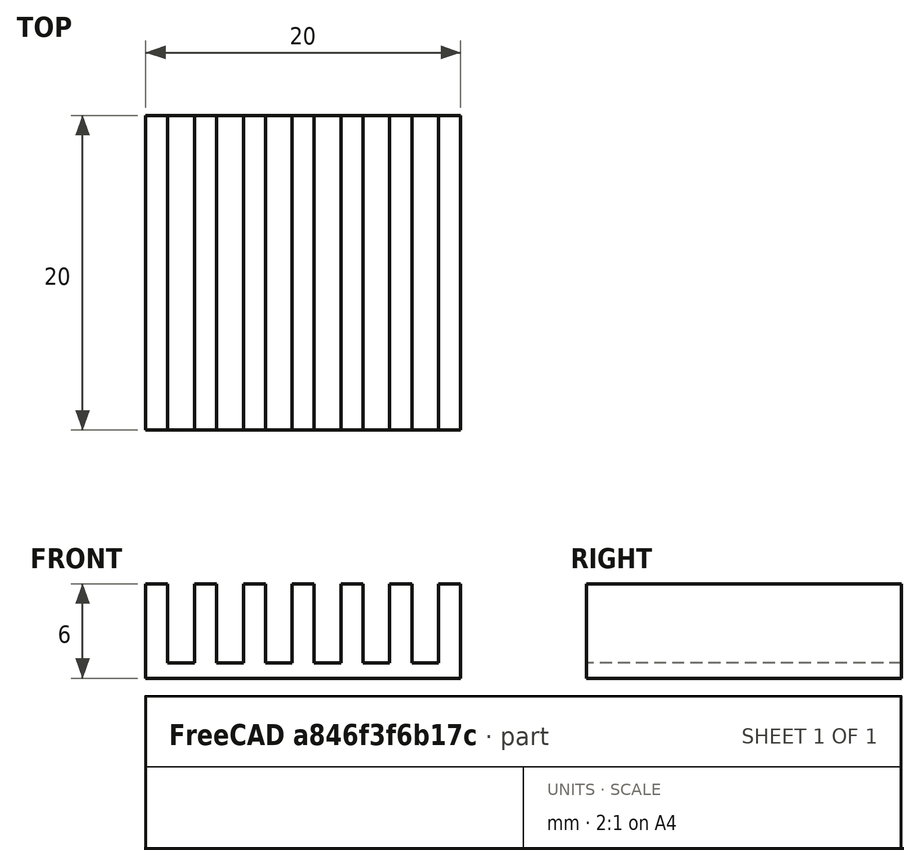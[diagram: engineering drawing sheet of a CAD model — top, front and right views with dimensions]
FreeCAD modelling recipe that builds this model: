
FCSTD DOCUMENT  (FreeCAD 0.16R5750 (Git))
Label: heatsink
License: All rights reserved
LicenseURL: http://en.wikipedia.org/wiki/All_rights_reserved
objects: Sketcher::SketchObject×1, PartDesign::Pad×1
note: 3 computed .brp shape members not serialized (recipe doc carries the construction recipe); baked Part::Feature solids carry a one-line shape summary decoded from their .brp

FEATURE [Sketcher::SketchObject] Sketch001  label="profilo001"
  Placement = pos=(0,0,0) rot=(-1,0,0;4.71239rad)
  sketch-geometry (28):
    g0: LineSegment StartX=0 StartY=0 StartZ=0 EndX=0 EndY=6 EndZ=0
    g1: LineSegment StartX=0 StartY=6 StartZ=0 EndX=1.4 EndY=6 EndZ=0
    g2: LineSegment StartX=1.4 StartY=6 StartZ=0 EndX=1.4 EndY=0.957608 EndZ=0
    g3: LineSegment StartX=1.4 StartY=0.957608 StartZ=0 EndX=3.1 EndY=0.957608 EndZ=0
    g4: LineSegment StartX=3.1 StartY=0.957608 StartZ=0 EndX=3.1 EndY=6 EndZ=0
    g5: LineSegment StartX=3.1 StartY=6 StartZ=0 EndX=4.5 EndY=6 EndZ=0
    g6: LineSegment StartX=4.5 StartY=6 StartZ=0 EndX=4.5 EndY=0.957608 EndZ=0
    g7: LineSegment StartX=4.5 StartY=0.957608 StartZ=0 EndX=6.2 EndY=0.957608 EndZ=0
    g8: LineSegment StartX=6.2 StartY=0.957608 StartZ=0 EndX=6.2 EndY=6 EndZ=0
    g9: LineSegment StartX=6.2 StartY=6 StartZ=0 EndX=7.6 EndY=6 EndZ=0
    g10: LineSegment StartX=7.6 StartY=6 StartZ=0 EndX=7.6 EndY=0.957608 EndZ=0
    g11: LineSegment StartX=7.6 StartY=0.957608 StartZ=0 EndX=9.3 EndY=0.957608 EndZ=0
    g12: LineSegment StartX=9.3 StartY=0.957608 StartZ=0 EndX=9.3 EndY=6 EndZ=0
    g13: LineSegment StartX=9.3 StartY=6 StartZ=0 EndX=10.7 EndY=6 EndZ=0
    g14: LineSegment StartX=10.7 StartY=6 StartZ=0 EndX=10.7 EndY=0.957608 EndZ=0
    g15: LineSegment StartX=10.7 StartY=0.957608 StartZ=0 EndX=12.4 EndY=0.957608 EndZ=0
    g16: LineSegment StartX=12.4 StartY=0.957608 StartZ=0 EndX=12.4 EndY=6 EndZ=0
    g17: LineSegment StartX=12.4 StartY=6 StartZ=0 EndX=13.8 EndY=6 EndZ=0
    g18: LineSegment StartX=13.8 StartY=6 StartZ=0 EndX=13.8 EndY=0.957608 EndZ=0
    g19: LineSegment StartX=13.8 StartY=0.957608 StartZ=0 EndX=15.5 EndY=0.957608 EndZ=0
    g20: LineSegment StartX=15.5 StartY=0.957608 StartZ=0 EndX=15.5 EndY=6 EndZ=0
    g21: LineSegment StartX=15.5 StartY=6 StartZ=0 EndX=16.9 EndY=6 EndZ=0
    g22: LineSegment StartX=16.9 StartY=6 StartZ=0 EndX=16.9 EndY=0.957608 EndZ=0
    g23: LineSegment StartX=16.9 StartY=0.957608 StartZ=0 EndX=18.6 EndY=0.957608 EndZ=0
    g24: LineSegment StartX=18.6 StartY=0.957608 StartZ=0 EndX=18.6 EndY=6 EndZ=0
    g25: LineSegment StartX=18.6 StartY=6 StartZ=0 EndX=20 EndY=6 EndZ=0
    g26: LineSegment StartX=20 StartY=6 StartZ=0 EndX=20 EndY=0 EndZ=0
    g27: LineSegment StartX=20 StartY=0 StartZ=0 EndX=0 EndY=0 EndZ=0
  constraints (83):
    c: Coincident(g-1,g0)
    c: Vertical(g0)
    c: Coincident(g0,g1)
    c: Coincident(g1,g2)
    c: Vertical(g2)
    c: Coincident(g2,g3)
    c: Horizontal(g3)
    c: Coincident(g3,g4)
    c: Vertical(g4)
    c: Coincident(g4,g5)
    c: Coincident(g5,g6)
    c: Vertical(g6)
    c: Coincident(g6,g7)
    c: Horizontal(g7)
    c: Coincident(g7,g8)
    c: Vertical(g8)
    c: Coincident(g8,g9)
    c: Coincident(g9,g10)
    c: Vertical(g10)
    c: Coincident(g10,g11)
    c: Coincident(g11,g12)
    c: Vertical(g12)
    c: Coincident(g12,g13)
    c: Coincident(g13,g14)
    c: Vertical(g14)
    c: Coincident(g14,g15)
    c: Coincident(g15,g16)
    c: Vertical(g16)
    c: Coincident(g16,g17)
    c: Coincident(g17,g18)
    c: Vertical(g18)
    c: Coincident(g18,g19)
    c: Coincident(g19,g20)
    c: Vertical(g20)
    c: Coincident(g20,g21)
    c: Coincident(g21,g22)
    c: Coincident(g22,g23)
    c: Coincident(g23,g24)
    c: Coincident(g24,g25)
    c: Coincident(g25,g26)
    c: Coincident(g26,g27)
    c: Coincident(g27,g0)
    c: Horizontal(g27)
    c: Equal(g0,g26)
    c: Equal(g1,g5)
    c: Equal(g5,g9)
    c: Equal(g9,g13)
    c: Equal(g13,g17)
    c: Equal(g17,g21)
    c: Equal(g21,g25)
    c: Equal(g3,g7)
    c: Equal(g7,g11)
    c: Equal(g11,g15)
    c: Equal(g15,g19)
    c: Equal(g19,g23)
    c: Horizontal(g1)
    c: Horizontal(g5)
    c: Horizontal(g9)
    c: Horizontal(g13)
    c: Horizontal(g17)
    c: Horizontal(g21)
    c: Horizontal(g25)
    c: Horizontal(g23)
    c: Horizontal(g19)
    c: Horizontal(g15)
    c: Horizontal(g11)
    c: Vertical(g22)
    c: Vertical(g24)
    c: Vertical(g26)
    c: DistanceY(g0) = 6
    c: DistanceX(g27) = -20
    c: Equal(g2,g4)
    c: Equal(g4,g6)
    c: Equal(g6,g8)
    c: Equal(g8,g10)
    c: Equal(g10,g12)
    c: Equal(g12,g14)
    c: Equal(g14,g16)
    c: Equal(g16,g18)
    c: Equal(g18,g20)
    c: Equal(g20,g22)
    c: Equal(g22,g24)
    c: DistanceX(g1) = 1.4
FEATURE [PartDesign::Pad] Pad  label="heatsink001"
  Length = 20
  Length2 = 100
  Placement = pos=(0,0,0) rot=(-1,0,0;4.71239rad)
  Sketch = -> Sketch001
  Type = 0
